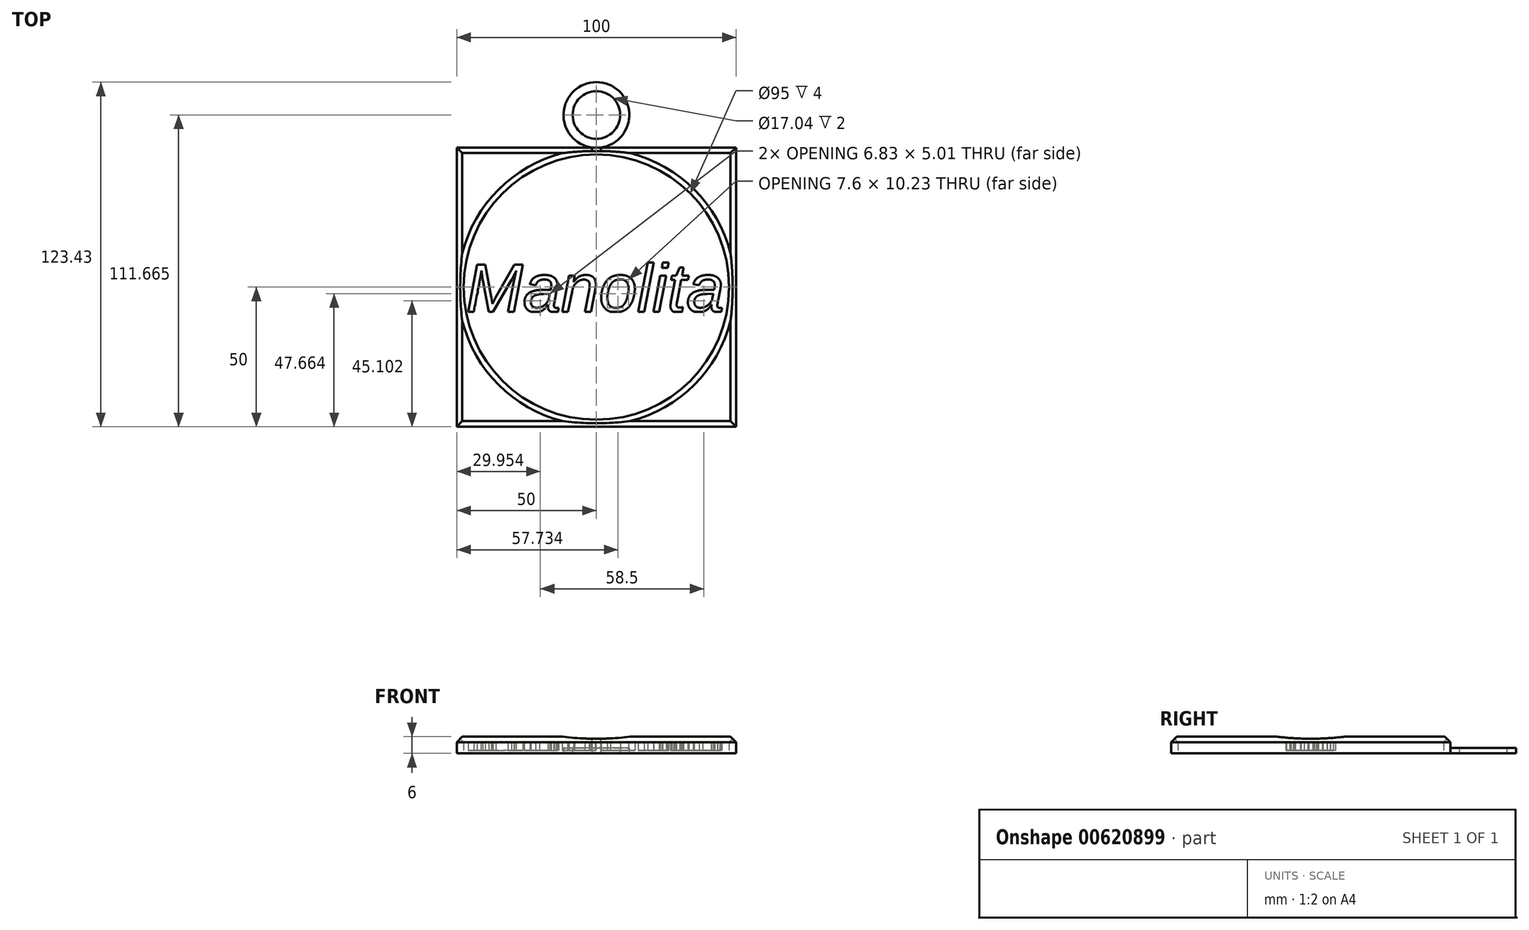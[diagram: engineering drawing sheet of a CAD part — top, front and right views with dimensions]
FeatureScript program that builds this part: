
annotation { "Feature Type Name" : "Feature", "Feature Type Description" : "" }
export const myFeature = defineFeature(function(context is Context, id is Id, definition is map)
    precondition{}
    {
        {
            var Q0;
            Q0=qCreatedBy(makeId("Top.planeOp"),FACE);
            var sketch = newSketch(context, id + "F0", { "sketchPlane" : qUnion([Q0])});
            skLineSegment(sketch, "E0.bottom", {"start": v(-50, -50) * mm, "end": v(50, -50) * mm});
            skLineSegment(sketch, "E0.top", {"start": v(-50, 50) * mm, "end": v(50, 50) * mm});
            skLineSegment(sketch, "E0.left", {"start": v(-50, -50) * mm, "end": v(-50, 50) * mm});
            skLineSegment(sketch, "E0.right", {"start": v(50, -50) * mm, "end": v(50, 50) * mm});
            skPoint(sketch, "E0.middle", {"position": v(0, 0) * mm});
            skCircle(sketch, "E1", {"center": v(0, 61.67) * mm, "radius": 11.77 * mm});
            skCircle(sketch, "E2", {"center": v(0, 61.67) * mm, "radius": 8.52 * mm});
            skCircle(sketch, "E3", {"center": v(0, 0) * mm, "radius": 47.5 * mm});
            skLineSegment(sketch, "E4.bottom", {"start": v(-46.68, -8.8) * mm, "end": v(46.68, -8.8) * mm});
            skLineSegment(sketch, "E4.top", {"start": v(-46.68, 8.8) * mm, "end": v(46.68, 8.8) * mm});
            skLineSegment(sketch, "E4.left", {"start": v(-46.68, -8.8) * mm, "end": v(-46.68, 8.8) * mm});
            skLineSegment(sketch, "E4.right", {"start": v(46.68, -8.8) * mm, "end": v(46.68, 8.8) * mm});
            skText(sketch, "E5", { "text": "Manolita", "fontName": "Arimo-Italic.ttf"});
            const initialGuessF0  = {"E5": [-0.04668, -0.0088, 1, 0, 0.01762]};
            skSetInitialGuess(sketch, initialGuessF0);
            skSolve(sketch);
        }
        {
            var Q0;
            Q0=makeQuery(id+"F0.imprint","IMPRINT",FACE,{"disambiguationData":[TD([[makeQuery(id+"F0.imprint","IMPRINT",EDGE,{"derivedFrom":sQuery(id+"F0.wireOp",EDGE,"E0.bottom")}),1.0]])]});
            extrude(context, id + "F1", {"entities" : qUnion([Q0]), "depth" : 5 * mm, "offsetDistance" : 25 * mm});
        }
        {
            var Q0;
            Q0=makeQuery(id+"F0.imprint","IMPRINT",FACE,{"disambiguationData":[TD([[makeQuery(id+"F0.imprint","IMPRINT",EDGE,{"derivedFrom":sQuery(id+"F0.wireOp",EDGE,"E2")}),-1.0]])]});
            var Q1;
            Q1 = qSketchRegion(id + "F0", true);
            extrude(context, id + "F2", {"entities" : qUnion([Q0, Q1]), "operationType" : NewBodyOperationType.ADD, "depth" : 1 * mm, "offsetDistance" : 25 * mm});
        }
        {
            var Q0;
            Q0=makeQuery(id+"F1.opExtrude","CAP_FACE",FACE,{"disambiguationData":[OSD([sQuery(id+"F0.wireOp",EDGE,"E0.bottom"),sQuery(id+"F0.wireOp",EDGE,"E0.top"),sQuery(id+"F0.wireOp",EDGE,"E0.left"),sQuery(id+"F0.wireOp",EDGE,"E0.right"),sQuery(id+"F0.wireOp",EDGE,"E1"),sQuery(id+"F0.wireOp",EDGE,"E3")])],"isStart":false});
            chamfer(context, id + "F3", {"entities" : qUnion([Q0]), "width" : 2 * mm, "tangentPropagation" : true});
        }
        {
            var Q0;
            Q0 = qSketchRegion(id + "F0", true);
            var Q1;
            Q1=makeQuery(id+"F2.opExtrude","CAP_FACE",FACE,{"disambiguationData":[OSD([sQuery(id+"F0.wireOp",EDGE,"E0.bottom"),sQuery(id+"F0.wireOp",EDGE,"E0.top"),sQuery(id+"F0.wireOp",EDGE,"E0.left"),sQuery(id+"F0.wireOp",EDGE,"E0.right"),sQuery(id+"F0.wireOp",EDGE,"E1"),sQuery(id+"F0.wireOp",EDGE,"E2"),sQuery(id+"F0.wireOp",EDGE,"E3")])],"isStart":false});
            extrude(context, id + "F4", {"entities" : qUnion([Q0, Q1]), "operationType" : NewBodyOperationType.ADD, "oppositeDirection" : true, "depth" : 1 * mm, "offsetDistance" : 25 * mm});
        }
        {
            var Q0;
            Q0=makeQuery(id+"F0.imprint","IMPRINT",FACE,{"disambiguationData":[TD([[makeQuery(id+"F0.imprint","IMPRINT",EDGE,{"derivedFrom":sQuery(id+"F0.wireOp",EDGE,"E5.sketch_text.stroke-107")}),-1.0]])]});
            var Q1;
            {var subQ5=sQuery(id+"F0.wireOp",EDGE,"E5.sketch_text.stroke-106");Q1=makeQuery(id+"F0.imprint","IMPRINT",FACE,{"disambiguationData":[TD([[makeQuery(id+"F0.imprint","IMPRINT",EDGE,{"derivedFrom":subQ5}),-1.0]])]});}
            var Q2;
            {var subQ5=sQuery(id+"F0.wireOp",EDGE,"E5.sketch_text.stroke-102");Q2=makeQuery(id+"F0.imprint","IMPRINT",FACE,{"disambiguationData":[TD([[makeQuery(id+"F0.imprint","IMPRINT",EDGE,{"derivedFrom":subQ5}),-1.0]])]});}
            var Q3;
            Q3=makeQuery(id+"F0.imprint","IMPRINT",FACE,{"disambiguationData":[TD([[makeQuery(id+"F0.imprint","IMPRINT",EDGE,{"derivedFrom":sQuery(id+"F0.wireOp",EDGE,"E5.sketch_text.stroke-0")}),-1.0]])]});
            var Q4;
            Q4=makeQuery(id+"F0.imprint","IMPRINT",FACE,{"disambiguationData":[TD([[makeQuery(id+"F0.imprint","IMPRINT",EDGE,{"derivedFrom":sQuery(id+"F0.wireOp",EDGE,"E5.sketch_text.stroke-58")}),-1.0]])]});
            var Q5;
            {var subQ0=sQuery(id+"F0.wireOp",EDGE,"E5.sketch_text.stroke-131");Q5=makeQuery(id+"F0.imprint","IMPRINT",FACE,{"disambiguationData":[TD([[makeQuery(id+"F0.imprint","IMPRINT",EDGE,{"derivedFrom":subQ0}),-1.0]])]});}
            var Q6;
            Q6=makeQuery(id+"F0.imprint","IMPRINT",FACE,{"disambiguationData":[TD([[makeQuery(id+"F0.imprint","IMPRINT",EDGE,{"derivedFrom":sQuery(id+"F0.wireOp",EDGE,"E5.sketch_text.stroke-78")}),-1.0]])]});
            var Q7;
            {var subQ0=sQuery(id+"F0.wireOp",EDGE,"E5.sketch_text.stroke-20");Q7=makeQuery(id+"F0.imprint","IMPRINT",FACE,{"disambiguationData":[TD([[makeQuery(id+"F0.imprint","IMPRINT",EDGE,{"derivedFrom":subQ0}),-1.0]])]});}
            var Q8;
            {var subQ5=sQuery(id+"F0.wireOp",EDGE,"E5.sketch_text.stroke-112");Q8=makeQuery(id+"F0.imprint","IMPRINT",FACE,{"disambiguationData":[TD([[makeQuery(id+"F0.imprint","IMPRINT",EDGE,{"derivedFrom":subQ5}),-1.0]])]});}
            extrude(context, id + "F5", {"entities" : qUnion([Q0, Q1, Q2, Q3, Q4, Q5, Q6, Q7, Q8]), "depth" : 3 * mm, "offsetDistance" : 25 * mm});
        }
        {
            var Q0;
            Q0=qCreatedBy(makeId("Top.planeOp"),FACE);
            var sketch = newSketch(context, id + "F6", { "sketchPlane" : qUnion([Q0])});
            skLineSegment(sketch, "E6", {"start": v(-46.53, -9) * mm, "end": v(47.53, -9) * mm});
            skLineSegment(sketch, "E7", {"start": v(46.87, 8.5) * mm, "end": v(-46.7, 8.5) * mm});
            skSolve(sketch);
        }
        {
            var Q0;
            {var subQ26=sQuery(id+"F0.wireOp",EDGE,"E5.sketch_text.stroke-4");Q0=makeQuery(id+"F0.imprint","IMPRINT",FACE,{"disambiguationData":[TD([[makeQuery(id+"F0.imprint","IMPRINT",EDGE,{"derivedFrom":subQ26}),1.0]])]});}
            var Q1;
            Q1=sQuery(id+"F6.wireOp",EDGE,"E7");
            extrude(context, id + "F7", {"entities" : qUnion([Q0]), "bodyType" : ToolBodyType.SURFACE, "surfaceEntities" : qUnion([Q1]), "depth" : 3 * mm, "offsetDistance" : 25 * mm});
        }
        {
            var Q0;
            Q0=qCreatedBy(makeId("Top.planeOp"),FACE);
            var sketch = newSketch(context, id + "F8", { "sketchPlane" : qUnion([Q0])});
            skLineSegment(sketch, "E8", {"start": v(-46.18, -9.05) * mm, "end": v(47.26, -9.05) * mm});
            skSolve(sketch);
        }
        {
            var Q0;
            Q0 = qSketchRegion(id + "F8", true);
            var Q1;
            Q1=sQuery(id+"F8.wireOp",EDGE,"E8");
            extrude(context, id + "F9", {"entities" : qUnion([Q0]), "bodyType" : ToolBodyType.SURFACE, "surfaceEntities" : qUnion([Q1]), "depth" : 3 * mm, "offsetDistance" : 25 * mm});
        }
    });
